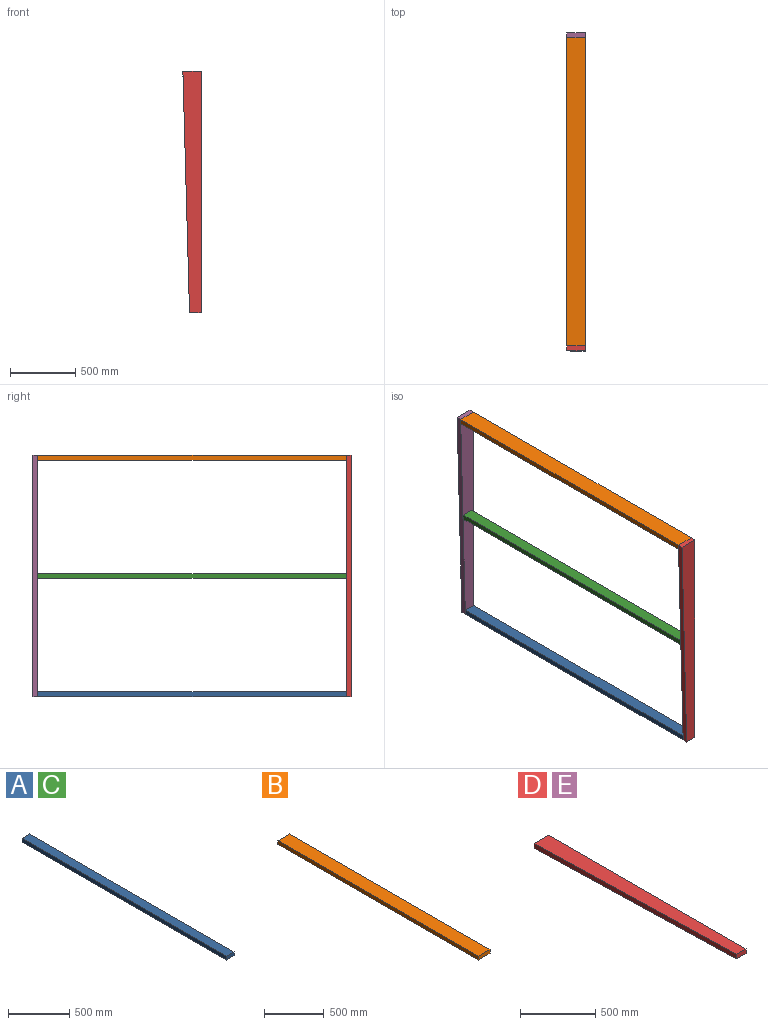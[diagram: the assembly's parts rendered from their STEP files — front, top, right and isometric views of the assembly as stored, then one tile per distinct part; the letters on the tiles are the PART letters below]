
ASSEMBLY  parts=5 mates=4
PART A: 6 faces, bbox 88.9x2362.2x38.1 mm
  f0: plane 2362.2x38.1mm, normal (-1,0,0), area 89999.8mm2, adj f1,f3,f4,f5
  f1: plane 2362.2x88.9mm, normal (0,0,-1), area 209999.6mm2, adj f0,f2,f4,f5
  f2: plane 2362.2x38.1mm, normal (1,0,0), area 89999.8mm2, adj f1,f3,f4,f5
  f3: plane 2362.2x88.9mm, normal (0,0,1), area 209999.6mm2, adj f0,f2,f4,f5
  f4: plane 88.9x38.1mm, normal (0,-1,0), area 3387.1mm2, adj f0,f1,f2,f3
  f5: plane 88.9x38.1mm, normal (0,1,0), area 3387.1mm2, adj f0,f1,f2,f3
PART B: 6 faces, bbox 139.7x2362.2x38.1 mm
  f0: plane 2362.2x139.7mm, normal (0,0,1), area 329999.3mm2, adj f1,f3,f4,f5
  f1: plane 2362.2x38.1mm, normal (-1,0,0), area 89999.8mm2, adj f0,f2,f4,f5
  f2: plane 2362.2x139.7mm, normal (0,0,-1), area 329999.3mm2, adj f1,f3,f4,f5
  f3: plane 2362.2x38.1mm, normal (1,0,0), area 89999.8mm2, adj f0,f2,f4,f5
  f4: plane 139.7x38.1mm, normal (0,-1,0), area 5322.6mm2, adj f0,f1,f2,f3
  f5: plane 139.7x38.1mm, normal (0,1,0), area 5322.6mm2, adj f0,f1,f2,f3
PART C: same geometry as A
PART D: 6 faces, bbox 139.7x1854.2x38.1 mm
  f0: plane 1854.2x139.7mm, normal (0,0,-1), area 211935.1mm2, adj f2,f3,f4,f5
  f1: plane 1854.2x139.7mm, normal (0,0,1), area 211935.1mm2, adj f2,f3,f4,f5
  f2: plane 1854.2x38.1mm, normal (1,0,0), area 70645mm2, adj f0,f1,f3,f4
  f3: plane 88.9x38.1mm, normal (0,-1,0), area 3387.1mm2, adj f0,f1,f2,f5
  f4: plane 139.7x38.1mm, normal (0,1,0), area 5322.6mm2, adj f0,f1,f2,f5
  f5: plane 1854.2x50.8mm, normal (-1,-0.03,0), area 70671.5mm2, adj f0,f1,f3,f4
PART E: same geometry as D
PLACE A rot(axis=(-1,0,0),180deg) t=(276.19,-2924.01,-1723.96)mm
PLACE B rot(axis=(-1,0,0),180deg) t=(250.79,-2924.01,92.14)mm
PLACE C t=(250.79,-561.81,-815.91)mm
PLACE D rot(axis=(1,0,0),90deg) t=(250.79,-2943.06,111.19)mm
PLACE E rot(axis=(1,0,0),90deg) t=(250.79,-542.76,111.19)mm
MATE fastened C.f5 <-> E.f1  axis (0,1,0) through (250.79,-561.81,-815.91)mm
MATE fastened B.f5 <-> D.f0  axis (0,-1,0) through (250.79,-2924.01,92.14)mm
MATE fastened B.f4 <-> E.f1  axis (0,1,0) through (250.79,-561.81,92.14)mm
MATE fastened A.f4 <-> E.f1  axis (0,1,0) through (276.19,-561.81,-1723.96)mm
